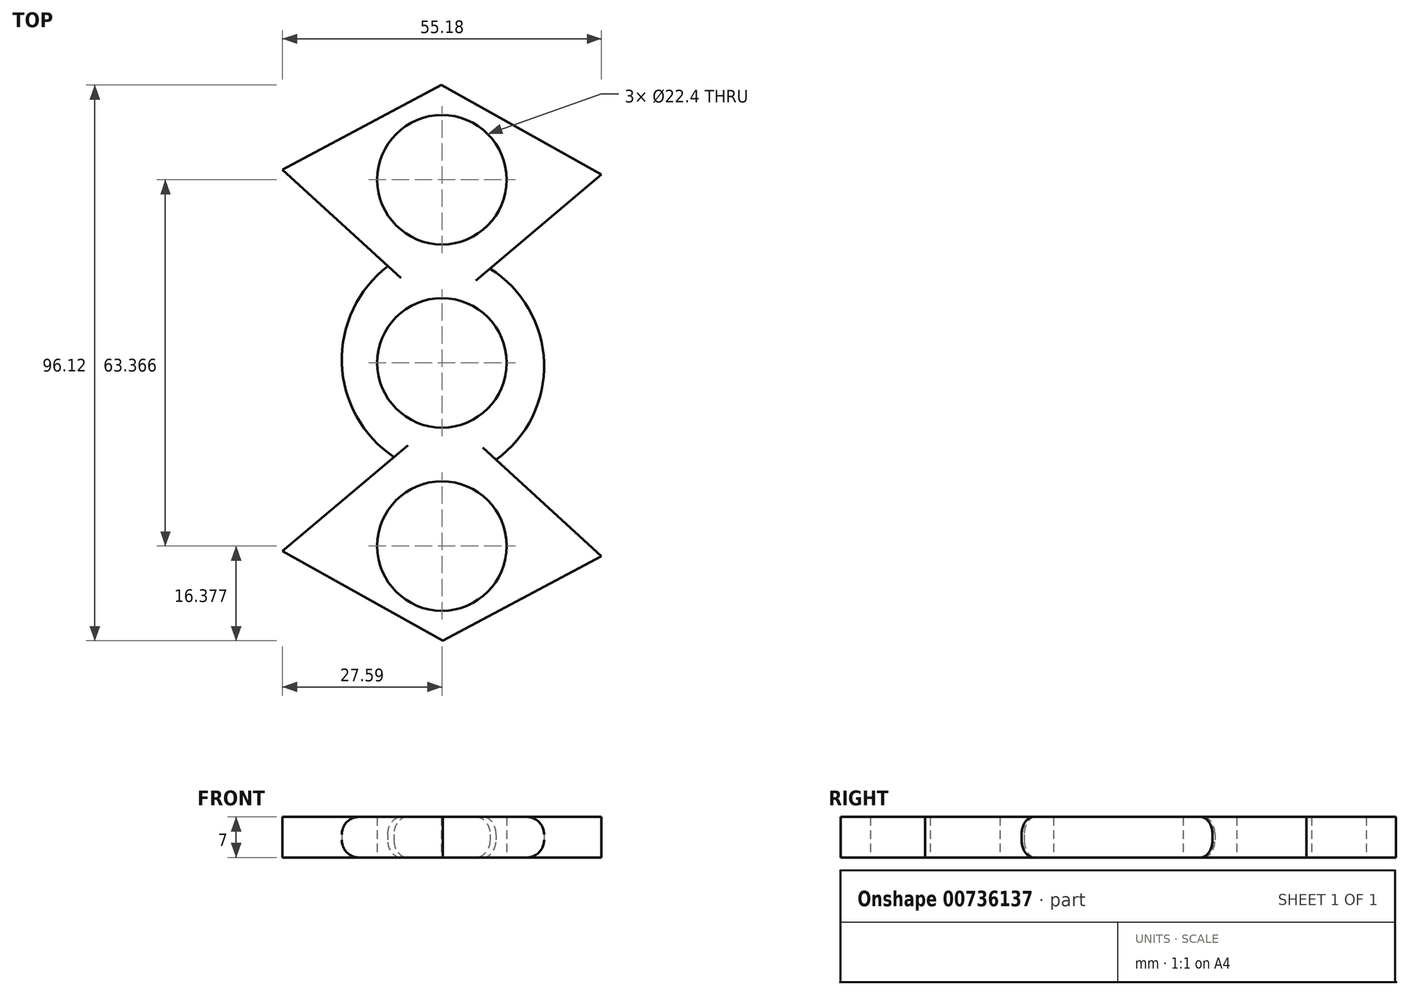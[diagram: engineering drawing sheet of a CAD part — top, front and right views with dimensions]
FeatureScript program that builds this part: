
annotation { "Feature Type Name" : "Feature", "Feature Type Description" : "" }
export const myFeature = defineFeature(function(context is Context, id is Id, definition is map)
    precondition{}
    {
        {
            var Q0;
            Q0=qCreatedBy(makeId("Top.planeOp"),FACE);
            var sketch = newSketch(context, id + "F0", { "sketchPlane" : qUnion([Q0])});
            skCircle(sketch, "E0", {"center": v(0, 0) * mm, "radius": 11.2 * mm});
            skLineSegment(sketch, "E1.0", {"start": v(27.6, 32.56) * mm, "end": v(8.31, 16.29) * mm});
            skLineSegment(sketch, "E1.1", {"start": v(8.31, 16.29) * mm, "end": v(-9.36, 16.73) * mm});
            skLineSegment(sketch, "E1.2", {"start": v(-9.36, 16.73) * mm, "end": v(-27.6, 33.43) * mm});
            skLineSegment(sketch, "E1.3", {"start": v(-27.6, 33.43) * mm, "end": v(-0.13, 48.06) * mm});
            skLineSegment(sketch, "E1.4", {"start": v(-0.13, 48.06) * mm, "end": v(27.6, 32.56) * mm});
            skCircle(sketch, "E2", {"center": v(0, 31.68) * mm, "radius": 11.2 * mm});
            skLineSegment(sketch, "E3.1.0", {"start": v(-8.31, -16.29) * mm, "end": v(9.36, -16.73) * mm});
            skLineSegment(sketch, "E3.1.1", {"start": v(-27.6, -32.56) * mm, "end": v(-8.31, -16.29) * mm});
            skLineSegment(sketch, "E3.1.2", {"start": v(9.36, -16.73) * mm, "end": v(27.6, -33.43) * mm});
            skLineSegment(sketch, "E3.1.3", {"start": v(27.6, -33.43) * mm, "end": v(0.13, -48.06) * mm});
            skLineSegment(sketch, "E3.1.4", {"start": v(0.13, -48.06) * mm, "end": v(-27.6, -32.56) * mm});
            skCircle(sketch, "E3.1.5", {"center": v(0, -31.68) * mm, "radius": 11.2 * mm});
            skArc(sketch, "E4", {"start": v(-9.36, 16.73) * mm, "mid": v(-17.32, -0.05) * mm, "end": v(-8.31, -16.29) * mm});
            skArc(sketch, "E5", {"start": v(9.36, -16.73) * mm, "mid": v(17.66, 0.06) * mm, "end": v(8.31, 16.29) * mm});
            skSolve(sketch);
        }
        {
            var Q0;
            Q0=makeQuery(id+"F0.imprint","IMPRINT",FACE,{"disambiguationData":[TD([[makeQuery(id+"F0.imprint","IMPRINT",EDGE,{"derivedFrom":sQuery(id+"F0.wireOp",EDGE,"E0")}),-1.0]])]});
            var Q1;
            Q1=makeQuery(id+"F0.imprint","IMPRINT",FACE,{"disambiguationData":[TD([[makeQuery(id+"F0.imprint","IMPRINT",EDGE,{"derivedFrom":sQuery(id+"F0.wireOp",EDGE,"E1.0")}),-1.0]])]});
            var Q2;
            Q2=makeQuery(id+"F0.imprint","IMPRINT",FACE,{"disambiguationData":[TD([[makeQuery(id+"F0.imprint","IMPRINT",EDGE,{"derivedFrom":sQuery(id+"F0.wireOp",EDGE,"E3.1.0")}),-1.0]])]});
            extrude(context, id + "F1", {"entities" : qUnion([Q0, Q1, Q2]), "depth" : 7 * mm, "offsetDistance" : 25 * mm});
        }
        {
            var Q0;
            Q0=makeQuery(id+"F1.opExtrude","CAP_EDGE",EDGE,{"disambiguationData":[OSD([sQuery(id+"F0.wireOp",EDGE,"E4")])],"isStart":false});
            var Q1;
            Q1=makeQuery(id+"F1.opExtrude","CAP_EDGE",EDGE,{"disambiguationData":[OSD([sQuery(id+"F0.wireOp",EDGE,"E5")])],"isStart":false});
            var Q2;
            Q2=makeQuery(id+"F1.opExtrude","CAP_EDGE",EDGE,{"disambiguationData":[OSD([sQuery(id+"F0.wireOp",EDGE,"E4")])],"isStart":true});
            var Q3;
            Q3=makeQuery(id+"F1.opExtrude","CAP_EDGE",EDGE,{"disambiguationData":[OSD([sQuery(id+"F0.wireOp",EDGE,"E5")])],"isStart":true});
            fillet(context, id + "F2", {"entities" : qUnion([Q0, Q1, Q2, Q3]), "radius" : 3 * mm, "tangentPropagation" : true, "allowEdgeOverflow" : false});
        }
    });
